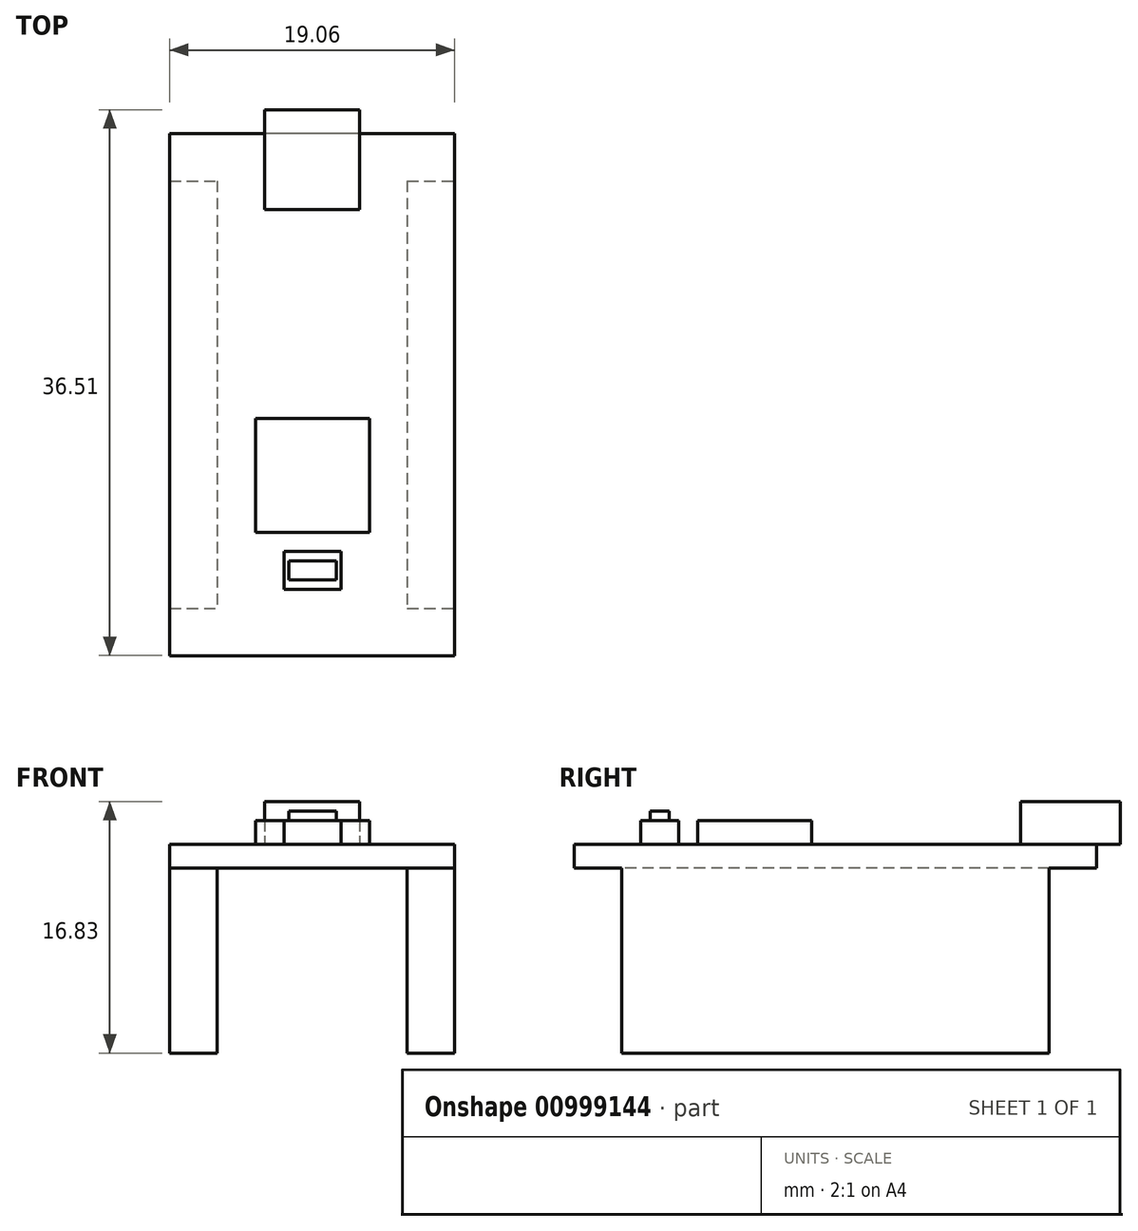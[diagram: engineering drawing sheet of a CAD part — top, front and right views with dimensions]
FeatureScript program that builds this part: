
annotation { "Feature Type Name" : "Feature", "Feature Type Description" : "" }
export const myFeature = defineFeature(function(context is Context, id is Id, definition is map)
    precondition{}
    {
        {
            var Q0;
            Q0=qCreatedBy(makeId("Top.planeOp"),FACE);
            var sketch = newSketch(context, id + "F0", { "sketchPlane" : qUnion([Q0])});
            skLineSegment(sketch, "E0.bottom", {"start": v(9.53, -17.46) * mm, "end": v(-9.52, -17.46) * mm});
            skLineSegment(sketch, "E0.top", {"start": v(9.52, 17.46) * mm, "end": v(-9.53, 17.46) * mm});
            skLineSegment(sketch, "E0.left", {"start": v(9.53, -17.46) * mm, "end": v(9.52, 17.46) * mm});
            skLineSegment(sketch, "E0.right", {"start": v(-9.52, -17.46) * mm, "end": v(-9.53, 17.46) * mm});
            skPoint(sketch, "E0.middle", {"position": v(0, 0) * mm});
            skLineSegment(sketch, "E1.bottom", {"start": v(-9.53, 17.46) * mm, "end": v(9.52, 17.46) * mm});
            skLineSegment(sketch, "E1.top", {"start": v(-9.53, 14.29) * mm, "end": v(9.52, 14.29) * mm});
            skLineSegment(sketch, "E1.left", {"start": v(-9.53, 17.46) * mm, "end": v(-9.53, 14.29) * mm});
            skLineSegment(sketch, "E1.right", {"start": v(9.52, 17.46) * mm, "end": v(9.52, 14.29) * mm});
            skLineSegment(sketch, "E2.bottom", {"start": v(-9.52, -17.46) * mm, "end": v(9.53, -17.46) * mm});
            skLineSegment(sketch, "E2.top", {"start": v(-9.52, -14.29) * mm, "end": v(9.53, -14.29) * mm});
            skLineSegment(sketch, "E2.left", {"start": v(-9.52, -17.46) * mm, "end": v(-9.52, -14.29) * mm});
            skLineSegment(sketch, "E2.right", {"start": v(9.53, -17.46) * mm, "end": v(9.53, -14.29) * mm});
            skLineSegment(sketch, "E3.bottom", {"start": v(-9.53, 14.29) * mm, "end": v(-6.35, 14.29) * mm});
            skLineSegment(sketch, "E3.top", {"start": v(-9.53, -14.29) * mm, "end": v(-6.35, -14.29) * mm});
            skLineSegment(sketch, "E3.left", {"start": v(-9.53, 14.29) * mm, "end": v(-9.53, -14.29) * mm});
            skLineSegment(sketch, "E3.right", {"start": v(-6.35, 14.29) * mm, "end": v(-6.35, -14.29) * mm});
            skLineSegment(sketch, "E4.bottom", {"start": v(9.52, 14.29) * mm, "end": v(6.35, 14.29) * mm});
            skLineSegment(sketch, "E4.top", {"start": v(9.52, -14.29) * mm, "end": v(6.35, -14.29) * mm});
            skLineSegment(sketch, "E4.left", {"start": v(9.52, 14.29) * mm, "end": v(9.52, -14.29) * mm});
            skLineSegment(sketch, "E4.right", {"start": v(6.35, 14.29) * mm, "end": v(6.35, -14.29) * mm});
            skLineSegment(sketch, "E5.bottom", {"start": v(9.53, -14.29) * mm, "end": v(3.83, -14.29) * mm});
            skLineSegment(sketch, "E5.top", {"start": v(9.53, -17.46) * mm, "end": v(3.81, -17.46) * mm});
            skLineSegment(sketch, "E5.left", {"start": v(9.53, -14.29) * mm, "end": v(9.53, -17.46) * mm});
            skLineSegment(sketch, "E6.bottom", {"start": v(-9.52, -14.29) * mm, "end": v(-3.8, -14.29) * mm});
            skLineSegment(sketch, "E6.top", {"start": v(-9.52, -17.46) * mm, "end": v(-3.8, -17.46) * mm});
            skLineSegment(sketch, "E6.left", {"start": v(-9.52, -14.29) * mm, "end": v(-9.52, -17.46) * mm});
            skLineSegment(sketch, "E6.right", {"start": v(-3.8, -14.29) * mm, "end": v(-3.8, -17.46) * mm});
            skLineSegment(sketch, "E7.bottom", {"start": v(9.53, -14.29) * mm, "end": v(3.81, -14.29) * mm});
            skLineSegment(sketch, "E7.right", {"start": v(3.81, -14.29) * mm, "end": v(3.81, -17.46) * mm});
            skLineSegment(sketch, "E8.bottom", {"start": v(3.83, -14.29) * mm, "end": v(-3.79, -14.29) * mm});
            skLineSegment(sketch, "E8.top", {"start": v(3.83, -1.59) * mm, "end": v(-3.79, -1.59) * mm});
            skLineSegment(sketch, "E8.left", {"start": v(3.83, -14.29) * mm, "end": v(3.83, -1.59) * mm});
            skLineSegment(sketch, "E8.right", {"start": v(-3.79, -14.29) * mm, "end": v(-3.79, -1.59) * mm});
            skLineSegment(sketch, "E9.bottom", {"start": v(9.52, 17.46) * mm, "end": v(3.17, 17.46) * mm});
            skLineSegment(sketch, "E9.top", {"start": v(9.52, 14.29) * mm, "end": v(3.17, 14.29) * mm});
            skLineSegment(sketch, "E9.right", {"start": v(3.17, 17.46) * mm, "end": v(3.17, 14.29) * mm});
            skLineSegment(sketch, "E10.bottom", {"start": v(-9.53, 17.46) * mm, "end": v(-3.18, 17.46) * mm});
            skLineSegment(sketch, "E10.top", {"start": v(-9.53, 14.29) * mm, "end": v(-3.18, 14.29) * mm});
            skLineSegment(sketch, "E10.right", {"start": v(-3.18, 17.46) * mm, "end": v(-3.18, 14.29) * mm});
            skLineSegment(sketch, "E11.bottom", {"start": v(-3.18, 17.46) * mm, "end": v(3.17, 17.46) * mm});
            skLineSegment(sketch, "E11.top", {"start": v(-3.18, 12.38) * mm, "end": v(3.17, 12.38) * mm});
            skLineSegment(sketch, "E11.left", {"start": v(-3.18, 17.46) * mm, "end": v(-3.18, 12.38) * mm});
            skLineSegment(sketch, "E11.right", {"start": v(3.17, 17.46) * mm, "end": v(3.17, 12.38) * mm});
            skLineSegment(sketch, "E12.top", {"start": v(-3.18, 19.05) * mm, "end": v(3.17, 19.05) * mm});
            skLineSegment(sketch, "E12.left", {"start": v(-3.18, 17.46) * mm, "end": v(-3.18, 19.05) * mm});
            skLineSegment(sketch, "E12.right", {"start": v(3.17, 17.46) * mm, "end": v(3.17, 19.05) * mm});
            skLineSegment(sketch, "E13.left", {"start": v(3.83, -1.59) * mm, "end": v(3.83, -9.2) * mm});
            skLineSegment(sketch, "E13.right", {"start": v(-3.79, -1.59) * mm, "end": v(-3.79, -9.2) * mm});
            skLineSegment(sketch, "E14.top", {"start": v(3.83, -9.2) * mm, "end": v(-3.79, -9.2) * mm});
            skLineSegment(sketch, "E15", {"start": v(9.53, -15.88) * mm, "end": v(0, -15.88) * mm});
            skLineSegment(sketch, "E16", {"start": v(0.02, -14.29) * mm, "end": v(0.02, -17.46) * mm});
            skLineSegment(sketch, "E17", {"start": v(0.02, -14.29) * mm, "end": v(0.02, -11.75) * mm});
            skLineSegment(sketch, "E18.bottom", {"start": v(1.93, -13.02) * mm, "end": v(-1.88, -13.02) * mm});
            skLineSegment(sketch, "E18.top", {"start": v(1.93, -10.48) * mm, "end": v(-1.88, -10.48) * mm});
            skLineSegment(sketch, "E18.left", {"start": v(1.93, -13.02) * mm, "end": v(1.93, -10.48) * mm});
            skLineSegment(sketch, "E18.right", {"start": v(-1.88, -13.02) * mm, "end": v(-1.88, -10.48) * mm});
            skPoint(sketch, "E18.middle", {"position": v(0.02, -11.75) * mm});
            skLineSegment(sketch, "E19.bottom", {"start": v(1.6, -11.11) * mm, "end": v(-1.57, -11.11) * mm});
            skLineSegment(sketch, "E19.top", {"start": v(1.6, -12.38) * mm, "end": v(-1.57, -12.38) * mm});
            skLineSegment(sketch, "E19.left", {"start": v(1.6, -11.11) * mm, "end": v(1.6, -12.38) * mm});
            skLineSegment(sketch, "E19.right", {"start": v(-1.57, -11.11) * mm, "end": v(-1.57, -12.38) * mm});
            skLineSegment(sketch, "E20", {"start": v(-6.35, 6.71) * mm, "end": v(6.35, 6.71) * mm});
            skSolve(sketch);
        }
        {
            var Q0;
            {var subQ0=sQuery(id+"F0.wireOp",EDGE,"E6.right");Q0=makeQuery(id+"F0.imprint","IMPRINT",FACE,{"disambiguationData":[TD([[makeQuery(id+"F0.imprint","IMPRINT",EDGE,{"derivedFrom":subQ0}),-1.0]])]});}
            var Q1;
            {var subQ1=sQuery(id+"F0.wireOp",EDGE,"E8.top");Q1=makeQuery(id+"F0.imprint","IMPRINT",FACE,{"disambiguationData":[TD([[makeQuery(id+"F0.imprint","IMPRINT",EDGE,{"derivedFrom":subQ1}),-1.0]])]});}
            var Q2;
            {var subQ4=sQuery(id+"F0.wireOp",EDGE,"E10.right");Q2=makeQuery(id+"F0.imprint","IMPRINT",FACE,{"disambiguationData":[TD([[makeQuery(id+"F0.imprint","IMPRINT",EDGE,{"derivedFrom":subQ4}),-1.0]])]});}
            var Q3;
            {var subQ0=sQuery(id+"F0.wireOp",EDGE,"E9.right");Q3=makeQuery(id+"F0.imprint","IMPRINT",FACE,{"disambiguationData":[TD([[makeQuery(id+"F0.imprint","IMPRINT",EDGE,{"derivedFrom":subQ0}),1.0]])]});}
            var Q4;
            {var subQ0=sQuery(id+"F0.wireOp",EDGE,"E0.left");var subQ1=sQuery(id+"F0.wireOp",EDGE,"E0.bottom");var subQ2=makeQuery(id+"F0.imprint","INTERSECT",VERTEX,{"derivedFrom":[subQ1,subQ0]});Q4=makeQuery(id+"F0.imprint","IMPRINT",FACE,{"disambiguationData":[TD([[makeQuery(id+"F0.imprint","IMPRINT",EDGE,{"disambiguationData":[TD([[subQ2,-1.0]])],"derivedFrom":subQ1}),-1.0]])]});}
            var Q5;
            {var subQ0=sQuery(id+"F0.wireOp",EDGE,"E16");var subQ1=sQuery(id+"F0.wireOp",EDGE,"E0.bottom");var subQ2=makeQuery(id+"F0.imprint","INTERSECT",VERTEX,{"derivedFrom":[subQ1,subQ0]});Q5=makeQuery(id+"F0.imprint","IMPRINT",FACE,{"disambiguationData":[TD([[makeQuery(id+"F0.imprint","IMPRINT",EDGE,{"disambiguationData":[TD([[subQ2,1.0]])],"derivedFrom":subQ1}),-1.0]])]});}
            var Q6;
            {var subQ0=sQuery(id+"F0.wireOp",EDGE,"E2.top");var subQ5=sQuery(id+"F0.wireOp",EDGE,"E0.left");var subQ8=makeQuery(id+"F0.imprint","INTERSECT",VERTEX,{"derivedFrom":[subQ5,subQ0]});Q6=makeQuery(id+"F0.imprint","IMPRINT",FACE,{"disambiguationData":[TD([[makeQuery(id+"F0.imprint","IMPRINT",EDGE,{"disambiguationData":[TD([[subQ8,1.0]])],"derivedFrom":subQ5}),1.0]])]});}
            var Q7;
            {var subQ0=sQuery(id+"F0.wireOp",EDGE,"E6.right");Q7=makeQuery(id+"F0.imprint","IMPRINT",FACE,{"disambiguationData":[TD([[makeQuery(id+"F0.imprint","IMPRINT",EDGE,{"derivedFrom":subQ0}),1.0]])]});}
            var Q8;
            {var subQ0=sQuery(id+"F0.wireOp",EDGE,"E7.right");var subQ1=sQuery(id+"F0.wireOp",EDGE,"E2.top");var subQ2=makeQuery(id+"F0.imprint","INTERSECT",VERTEX,{"derivedFrom":[subQ1,subQ0]});Q8=makeQuery(id+"F0.imprint","IMPRINT",FACE,{"disambiguationData":[TD([[makeQuery(id+"F0.imprint","IMPRINT",EDGE,{"disambiguationData":[TD([[subQ2,1.0]])],"derivedFrom":subQ1}),-1.0]])]});}
            var Q9;
            {var subQ4=sQuery(id+"F0.wireOp",EDGE,"E14.top");Q9=makeQuery(id+"F0.imprint","IMPRINT",FACE,{"disambiguationData":[TD([[makeQuery(id+"F0.imprint","IMPRINT",EDGE,{"derivedFrom":subQ4}),1.0]])]});}
            var Q10;
            Q10=makeQuery(id+"F0.imprint","IMPRINT",FACE,{"disambiguationData":[TD([[makeQuery(id+"F0.imprint","IMPRINT",EDGE,{"derivedFrom":sQuery(id+"F0.wireOp",EDGE,"E11.top")}),-1.0]])]});
            extrude(context, id + "F1", {"entities" : qUnion([Q0, Q1, Q2, Q3, Q4, Q5, Q6, Q7, Q8, Q9, Q10]), "depth" : 1.59 * mm, "offsetDistance" : 25.4 * mm});
        }
        {
            var Q0;
            {var subQ2=sQuery(id+"F0.wireOp",EDGE,"E9.right");Q0=makeQuery(id+"F0.imprint","IMPRINT",FACE,{"disambiguationData":[TD([[makeQuery(id+"F0.imprint","IMPRINT",EDGE,{"derivedFrom":subQ2}),-1.0]])]});}
            var Q1;
            Q1=makeQuery(id+"F0.imprint","IMPRINT",FACE,{"disambiguationData":[TD([[makeQuery(id+"F0.imprint","IMPRINT",EDGE,{"derivedFrom":sQuery(id+"F0.wireOp",EDGE,"E11.top")}),1.0]])]});
            extrude(context, id + "F2", {"entities" : qUnion([Q0, Q1]), "operationType" : NewBodyOperationType.ADD, "depth" : 4.44 * mm, "offsetDistance" : 25.4 * mm});
        }
        {
            var Q0;
            Q0=makeQuery(id+"F0.imprint","IMPRINT",FACE,{"disambiguationData":[TD([[makeQuery(id+"F0.imprint","IMPRINT",EDGE,{"derivedFrom":sQuery(id+"F0.wireOp",EDGE,"E12.top")}),-1.0]])]});
            extrude(context, id + "F3", {"entities" : qUnion([Q0]), "operationType" : NewBodyOperationType.ADD, "depth" : 4.44 * mm, "offsetDistance" : 25.4 * mm});
        }
        {
            var Q0;
            Q0=makeQuery(id+"F0.imprint","IMPRINT",FACE,{"disambiguationData":[TD([[makeQuery(id+"F0.imprint","IMPRINT",EDGE,{"derivedFrom":sQuery(id+"F0.wireOp",EDGE,"E12.top")}),-1.0]])]});
            extrude(context, id + "F4", {"entities" : qUnion([Q0]), "operationType" : NewBodyOperationType.REMOVE, "depth" : 1.59 * mm, "offsetDistance" : 25.4 * mm});
        }
        {
            var Q0;
            {var subQ2=sQuery(id+"F0.wireOp",EDGE,"E2.top");var subQ5=sQuery(id+"F0.wireOp",EDGE,"E0.right");var subQ8=makeQuery(id+"F0.imprint","INTERSECT",VERTEX,{"derivedFrom":[subQ5,subQ2]});Q0=makeQuery(id+"F0.imprint","IMPRINT",FACE,{"disambiguationData":[TD([[makeQuery(id+"F0.imprint","IMPRINT",EDGE,{"disambiguationData":[TD([[subQ8,-1.0]])],"derivedFrom":subQ5}),-1.0]])]});}
            var Q1;
            {var subQ2=sQuery(id+"F0.wireOp",EDGE,"E2.top");var subQ4=sQuery(id+"F0.wireOp",EDGE,"E0.left");var subQ5=makeQuery(id+"F0.imprint","INTERSECT",VERTEX,{"derivedFrom":[subQ4,subQ2]});Q1=makeQuery(id+"F0.imprint","IMPRINT",FACE,{"disambiguationData":[TD([[makeQuery(id+"F0.imprint","IMPRINT",EDGE,{"disambiguationData":[TD([[subQ5,-1.0]])],"derivedFrom":subQ4}),1.0]])]});}
            extrude(context, id + "F5", {"entities" : qUnion([Q0, Q1]), "operationType" : NewBodyOperationType.ADD, "depth" : 1.59 * mm, "offsetDistance" : 25.4 * mm});
        }
        {
            var Q0;
            {var subQ2=sQuery(id+"F0.wireOp",EDGE,"E2.top");var subQ4=sQuery(id+"F0.wireOp",EDGE,"E0.left");var subQ5=makeQuery(id+"F0.imprint","INTERSECT",VERTEX,{"derivedFrom":[subQ4,subQ2]});Q0=makeQuery(id+"F0.imprint","IMPRINT",FACE,{"disambiguationData":[TD([[makeQuery(id+"F0.imprint","IMPRINT",EDGE,{"disambiguationData":[TD([[subQ5,-1.0]])],"derivedFrom":subQ4}),1.0]])]});}
            var Q1;
            {var subQ2=sQuery(id+"F0.wireOp",EDGE,"E2.top");var subQ5=sQuery(id+"F0.wireOp",EDGE,"E0.right");var subQ8=makeQuery(id+"F0.imprint","INTERSECT",VERTEX,{"derivedFrom":[subQ5,subQ2]});Q1=makeQuery(id+"F0.imprint","IMPRINT",FACE,{"disambiguationData":[TD([[makeQuery(id+"F0.imprint","IMPRINT",EDGE,{"disambiguationData":[TD([[subQ8,-1.0]])],"derivedFrom":subQ5}),-1.0]])]});}
            extrude(context, id + "F6", {"entities" : qUnion([Q0, Q1]), "operationType" : NewBodyOperationType.ADD, "oppositeDirection" : true, "depth" : 12.38 * mm, "offsetDistance" : 25.4 * mm});
        }
        {
            var Q0;
            Q0=makeQuery(id+"F0.imprint","IMPRINT",FACE,{"disambiguationData":[TD([[makeQuery(id+"F0.imprint","IMPRINT",EDGE,{"derivedFrom":sQuery(id+"F0.wireOp",EDGE,"E18.top")}),1.0]])]});
            extrude(context, id + "F7", {"entities" : qUnion([Q0]), "operationType" : NewBodyOperationType.ADD, "depth" : 3.17 * mm, "offsetDistance" : 25.4 * mm});
        }
        {
            var Q0;
            Q0=makeQuery(id+"F0.imprint","IMPRINT",FACE,{"disambiguationData":[TD([[makeQuery(id+"F0.imprint","IMPRINT",EDGE,{"derivedFrom":sQuery(id+"F0.wireOp",EDGE,"E19.bottom")}),1.0]])]});
            extrude(context, id + "F8", {"entities" : qUnion([Q0]), "operationType" : NewBodyOperationType.ADD, "depth" : 3.8 * mm, "offsetDistance" : 25.4 * mm});
        }
        {
            var Q0;
            {var subQ0=sQuery(id+"F0.wireOp",EDGE,"E8.top");Q0=makeQuery(id+"F0.imprint","IMPRINT",FACE,{"disambiguationData":[TD([[makeQuery(id+"F0.imprint","IMPRINT",EDGE,{"derivedFrom":subQ0}),1.0]])]});}
            extrude(context, id + "F9", {"entities" : qUnion([Q0]), "operationType" : NewBodyOperationType.ADD, "depth" : 3.17 * mm, "offsetDistance" : 25.4 * mm});
        }
    });
